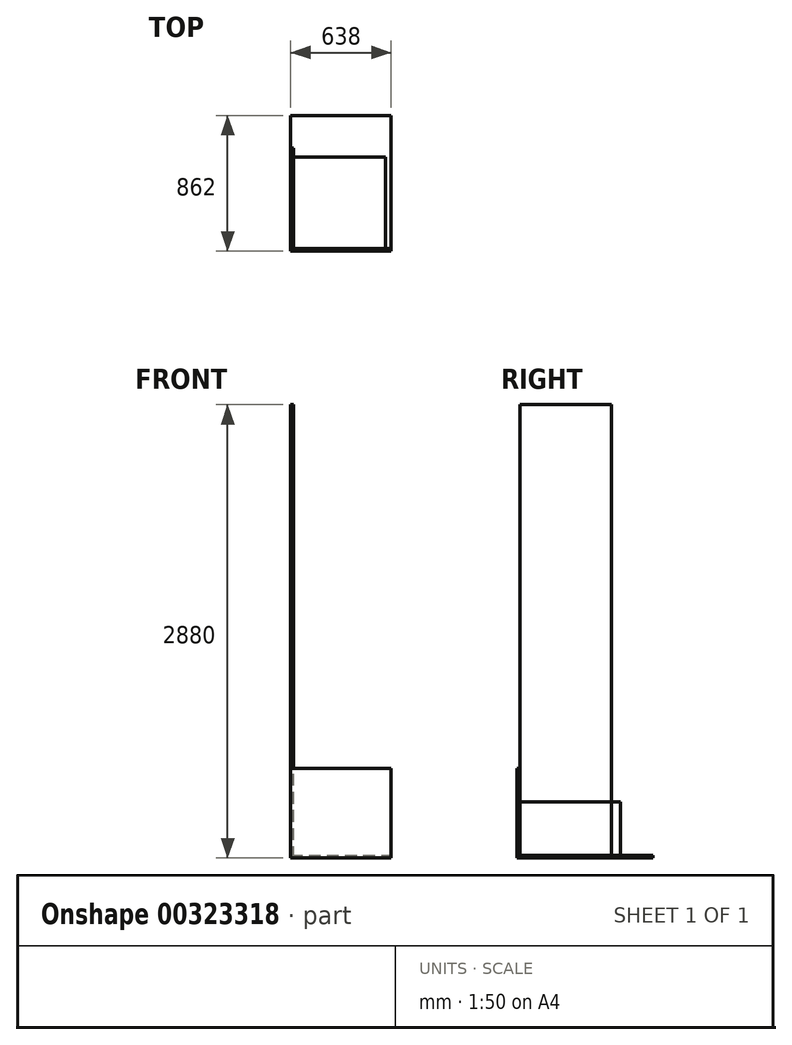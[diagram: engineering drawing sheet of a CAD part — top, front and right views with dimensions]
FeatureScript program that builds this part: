
annotation { "Feature Type Name" : "Feature", "Feature Type Description" : "" }
export const myFeature = defineFeature(function(context is Context, id is Id, definition is map)
    precondition{}
    {
        {
            var Q0;
            Q0=qCreatedBy(makeId("Right.planeOp"),FACE);
            var sketch = newSketch(context, id + "F0", { "sketchPlane" : qUnion([Q0])});
            skLineSegment(sketch, "E0.bottom", {"start": v(0, 0) * mm, "end": v(580, 0) * mm});
            skLineSegment(sketch, "E0.top", {"start": v(0, 2880) * mm, "end": v(580, 2880) * mm});
            skLineSegment(sketch, "E0.left", {"start": v(0, 0) * mm, "end": v(0, 2880) * mm});
            skLineSegment(sketch, "E0.right", {"start": v(580, 0) * mm, "end": v(580, 2880) * mm});
            skSolve(sketch);
        }
        {
            var Q0;
            Q0 = qSketchRegion(id + "F0", true);
            extrude(context, id + "F1", {"entities" : qUnion([Q0]), "depth" : 18 * mm});
        }
        {
            var Q0;
            Q0=qCreatedBy(makeId("Top.planeOp"), FACE);
            var sketch = newSketch(context, id + "F2", { "sketchPlane" : qUnion([Q0])});
            skLineSegment(sketch, "E1.bottom", {"start": v(0, 0) * mm, "end": v(603, 0) * mm});
            skLineSegment(sketch, "E1.top", {"start": v(0, 580) * mm, "end": v(603, 580) * mm});
            skLineSegment(sketch, "E1.left", {"start": v(0, 0) * mm, "end": v(0, 580) * mm});
            skLineSegment(sketch, "E1.right", {"start": v(603, 0) * mm, "end": v(603, 580) * mm});
            skSolve(sketch);
        }
        {
            var Q0;
            Q0 = qSketchRegion(id + "F2", true);
            extrude(context, id + "F3", {"entities" : qUnion([Q0]), "domain" : OperationDomain.MODEL, "flatOperationType" : FlatOperationType.REMOVE, "depth" : 18 * mm, "offsetDistance" : 25 * mm});
        }
        {
            var Q0;
            Q0=qCreatedBy(makeId("Top.planeOp"), FACE);
            var sketch = newSketch(context, id + "F4", { "sketchPlane" : qUnion([Q0])});
            skLineSegment(sketch, "E2.bottom", {"start": v(0, 0) * mm, "end": v(638, 0) * mm});
            skLineSegment(sketch, "E2.top", {"start": v(0, 844) * mm, "end": v(638, 844) * mm});
            skLineSegment(sketch, "E2.left", {"start": v(0, 0) * mm, "end": v(0, 844) * mm});
            skLineSegment(sketch, "E2.right", {"start": v(638, 0) * mm, "end": v(638, 844) * mm});
            skSolve(sketch);
        }
        {
            var Q0;
            Q0 = qSketchRegion(id + "F4", true);
            extrude(context, id + "F5", {"entities" : qUnion([Q0]), "domain" : OperationDomain.MODEL, "flatOperationType" : FlatOperationType.REMOVE, "depth" : 18 * mm, "offsetDistance" : 25 * mm});
        }
        {
            var Q0;
            Q0=qCreatedBy(makeId("Front.planeOp"), FACE);
            var sketch = newSketch(context, id + "F6", { "sketchPlane" : qUnion([Q0])});
            skLineSegment(sketch, "E3.bottom", {"start": v(0, 0) * mm, "end": v(638, 0) * mm});
            skLineSegment(sketch, "E3.top", {"start": v(0, 570) * mm, "end": v(638, 570) * mm});
            skLineSegment(sketch, "E3.left", {"start": v(0, 0) * mm, "end": v(0, 570) * mm});
            skLineSegment(sketch, "E3.right", {"start": v(638, 0) * mm, "end": v(638, 570) * mm});
            skSolve(sketch);
        }
        {
            var Q0;
            Q0 = qSketchRegion(id + "F6", true);
            extrude(context, id + "F7", {"entities" : qUnion([Q0]), "domain" : OperationDomain.MODEL, "flatOperationType" : FlatOperationType.REMOVE, "depth" : 18 * mm, "offsetDistance" : 25 * mm});
        }
        {
            var Q0;
            Q0=qCreatedBy(makeId("Right.planeOp"), FACE);
            var sketch = newSketch(context, id + "F8", { "sketchPlane" : qUnion([Q0])});
            skLineSegment(sketch, "E4.bottom", {"start": v(0, 0) * mm, "end": v(638, 0) * mm});
            skLineSegment(sketch, "E4.top", {"start": v(0, 356) * mm, "end": v(638, 356) * mm});
            skLineSegment(sketch, "E4.left", {"start": v(0, 0) * mm, "end": v(0, 356) * mm});
            skLineSegment(sketch, "E4.right", {"start": v(638, 0) * mm, "end": v(638, 356) * mm});
            skSolve(sketch);
        }
        {
            var Q0;
            Q0 = qSketchRegion(id + "F8", true);
            extrude(context, id + "F9", {"entities" : qUnion([Q0]), "domain" : OperationDomain.MODEL, "flatOperationType" : FlatOperationType.REMOVE, "depth" : 18 * mm, "offsetDistance" : 25 * mm});
        }
    });
